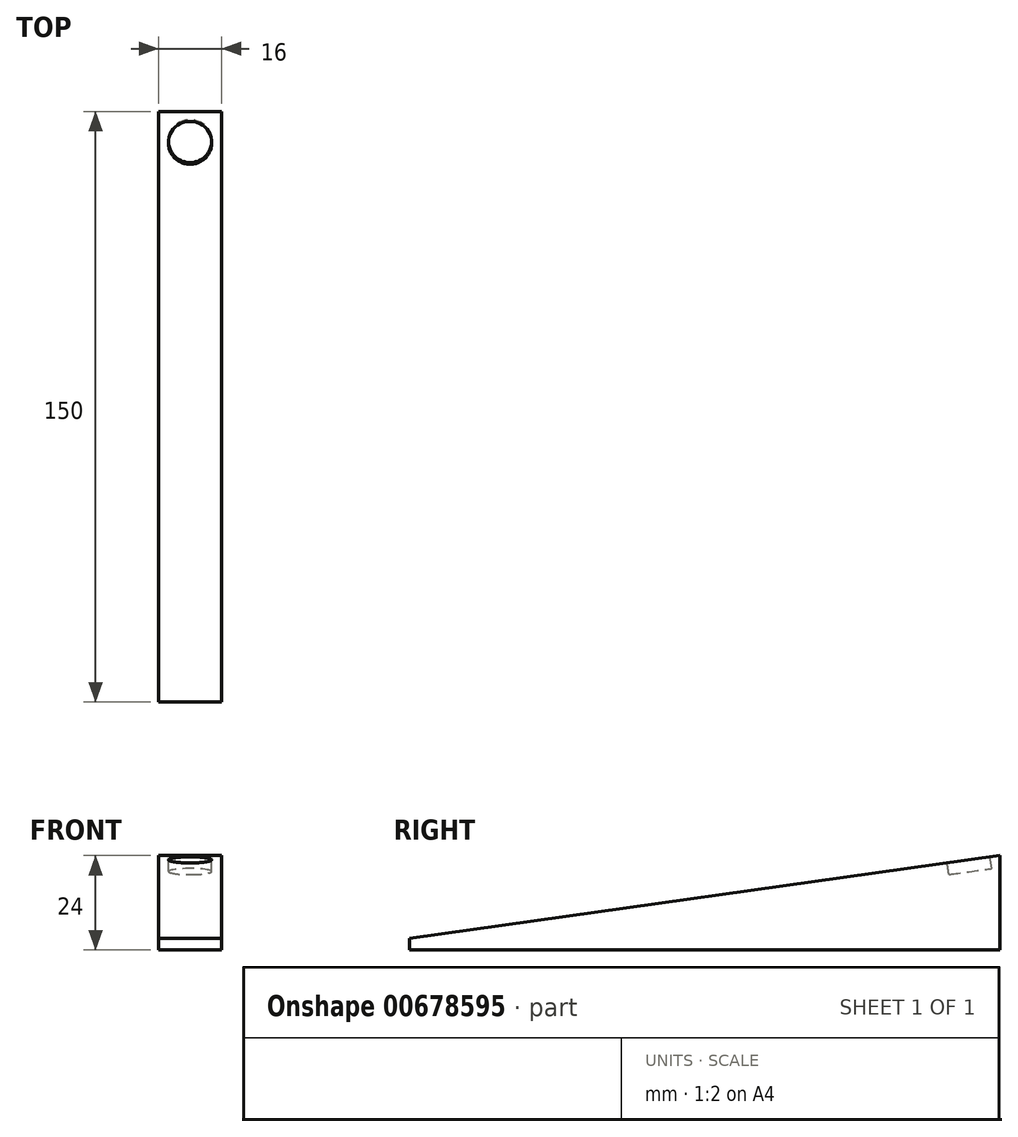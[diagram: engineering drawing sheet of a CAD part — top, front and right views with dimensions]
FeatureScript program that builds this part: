
annotation { "Feature Type Name" : "Feature", "Feature Type Description" : "" }
export const myFeature = defineFeature(function(context is Context, id is Id, definition is map)
    precondition{}
    {
        {
            var Q0;
            Q0=qCreatedBy(makeId("Top.planeOp"),FACE);
            var sketch = newSketch(context, id + "F0", { "sketchPlane" : qUnion([Q0])});
            skLineSegment(sketch, "E0.bottom", {"start": v(0, 0) * mm, "end": v(16, 0) * mm});
            skLineSegment(sketch, "E0.top", {"start": v(0, 150) * mm, "end": v(16, 150) * mm});
            skLineSegment(sketch, "E0.left", {"start": v(0, 0) * mm, "end": v(0, 150) * mm});
            skLineSegment(sketch, "E0.right", {"start": v(16, 0) * mm, "end": v(16, 150) * mm});
            skSolve(sketch);
        }
        {
            var Q0;
            Q0=makeQuery(id+"F0.imprint","IMPRINT",FACE,{"disambiguationData":[TD([[makeQuery(id+"F0.imprint","IMPRINT",EDGE,{"derivedFrom":sQuery(id+"F0.wireOp",EDGE,"E0.bottom")}),1.0]])]});
            extrude(context, id + "F1", {"entities" : qUnion([Q0]), "depth" : 24 * mm, "offsetDistance" : 25 * mm});
        }
        {
            var Q0;
            Q0=makeQuery(id+"F1.opExtrude","CAP_EDGE",EDGE,{"disambiguationData":[OSD([sQuery(id+"F0.wireOp",EDGE,"E0.bottom")])],"isStart":false});
            chamfer(context, id + "F2", {"entities" : qUnion([Q0]), "chamferType" : ChamferType.OFFSET_ANGLE, "width" : 150 * mm, "oppositeDirection" : false, "angle" : 8 * degree, "tangentPropagation" : true});
        }
        {
            var Q0;
            Q0=makeQuery(id+"F2.opChamfer","BLEND_FACE",FACE,{"disambiguationData":[OSD([sQuery(id+"F0.wireOp",EDGE,"E0.bottom")])]});
            var sketch = newSketch(context, id + "F3", { "sketchPlane" : qUnion([Q0])});
            skCircle(sketch, "E1", {"center": v(8, 143.88) * mm, "radius": 5.5 * mm});
            skSolve(sketch);
        }
        {
            var Q0;
            Q0=makeQuery(id+"F3.imprint","IMPRINT",FACE,{"disambiguationData":[TD([[makeQuery(id+"F3.imprint","IMPRINT",EDGE,{"derivedFrom":sQuery(id+"F3.wireOp",EDGE,"E1")}),1.0]])]});
            extrude(context, id + "F4", {"entities" : qUnion([Q0]), "operationType" : NewBodyOperationType.REMOVE, "oppositeDirection" : true, "depth" : 3 * mm, "offsetDistance" : 25 * mm});
        }
    });
